# Revit family: 79X
name_source: partatom
category: Lighting Fixtures
revit_build: Autodesk Revit 2014 (Build: 20130308_1515(x64)
units: mm (PartAtom-declared; Revit-internal decimal feet)

## types (4) — shared parameters
Apparent Load = 0 VA
Assembly Code = D5020200
Color Filter = 16777215
Default Elevation = 48"
Description = 6 Inch PARABOLIC AND BAFFLE DOWNLIGHTS
Dimming Lamp Color Temperature Shift = <None>
Emit Shape Visible in Rendering = No
Emit from Circle Diameter = 6"
Housing Material = Paint - Hubbell - Black
Lamp = PAR38 Lamp
Load Classification = Lighting
Manufacturer = Prescolite
Model = 79X
Power Factor = 1
Product Page URL = https://www.hubbell.com
Reflector Finish = Steel - Hubbell
Tilt Angle = -90.00°
URL = https://www.hubbell.com
Voltage = 120 V
Wattage Comments = 75-150 W

## per-type parameters (varying)
| type | Photometric Web File | Product Specification Sheet | Watts |
| 79X-ST832_150W_PAR38_FLOOD | 79x-st832_150w_par38_flood.ies | http://www.prescolite.com | 150 W |
| 79X-ST832_150W_PAR38_SPOT | 79x-st832_150w_par38_spot.ies | http://www.prescolite.com | 150 W |
| 79X-ST832_75W_R30_FLOOD | 79x-st832_75w_r30_flood.ies | https://hubbellcdn.com | 75 W |
| 79X-ST832_75W_R30_SPOT | 79x-st832_75w_r30_spot.ies | http://www.prescolite.com | 75 W |

## geometry (parser evidence)
native form markers: Blend x5, Sweep x1
no freeform markers — native parametric forms only
